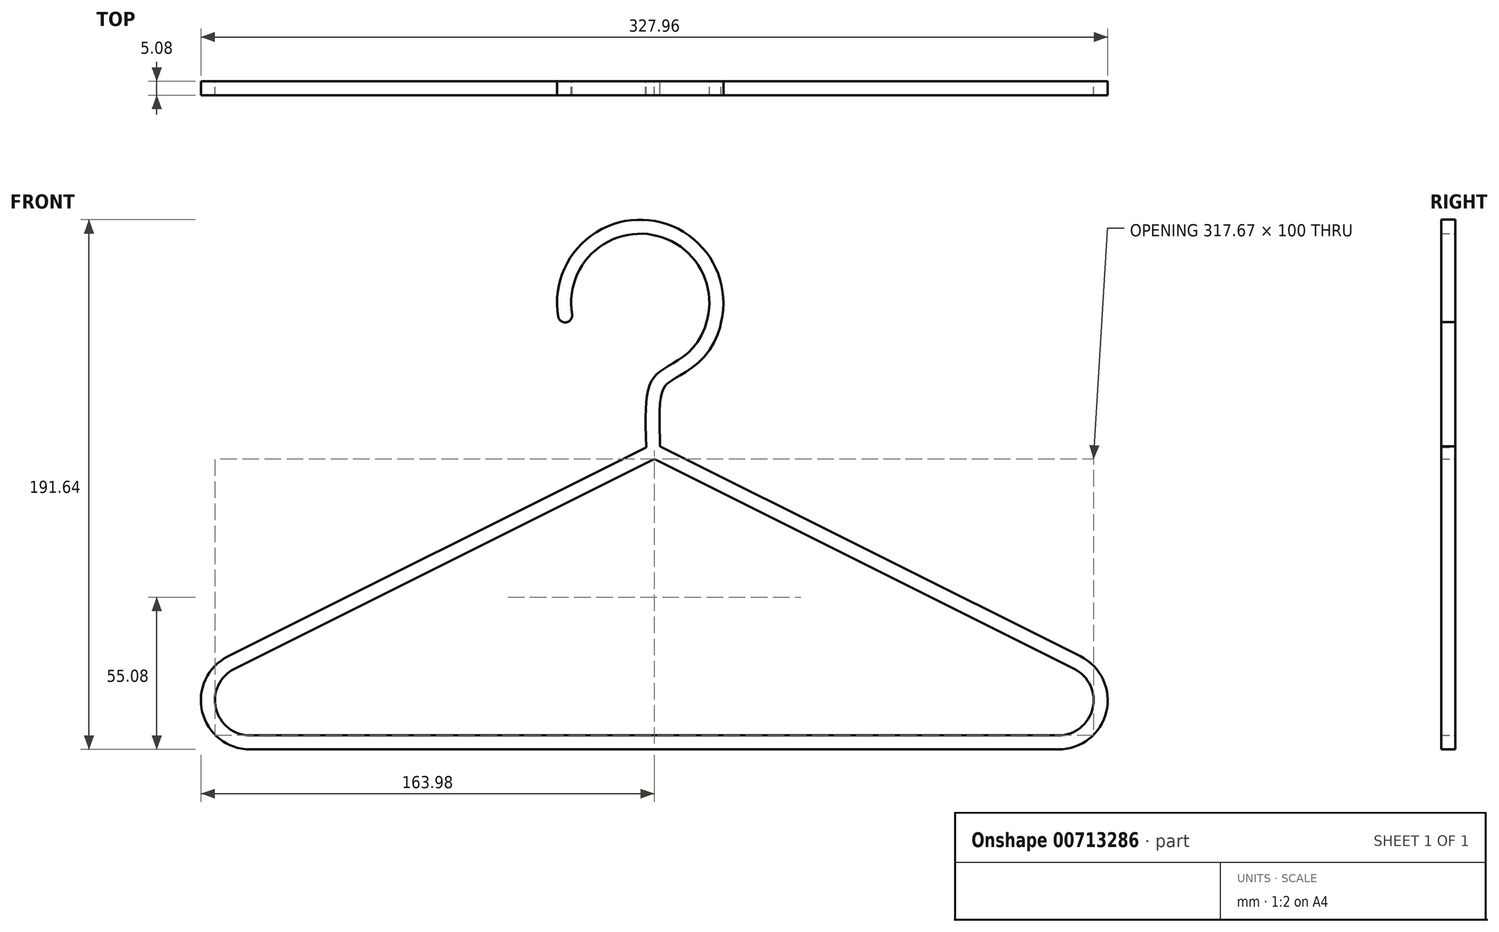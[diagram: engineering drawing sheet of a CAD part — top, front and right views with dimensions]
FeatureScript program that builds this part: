
annotation { "Feature Type Name" : "Feature", "Feature Type Description" : "" }
export const myFeature = defineFeature(function(context is Context, id is Id, definition is map)
    precondition{}
    {
        {
            var Q0;
            Q0=qCreatedBy(makeId("Front.planeOp"),FACE);
            var sketch = newSketch(context, id + "F0", { "sketchPlane" : qUnion([Q0])});
            skLineSegment(sketch, "E0", {"start": v(-146.2, 5.08) * mm, "end": v(146.2, 5.08) * mm});
            skLineSegment(sketch, "E1", {"start": v(151.88, 29.14) * mm, "end": v(0, 105.08) * mm});
            skLineSegment(sketch, "E2", {"start": v(0, 105.08) * mm, "end": v(-151.88, 29.14) * mm});
            skPoint(sketch, "E3.visualSharp", {"position": v(-200, 5.08) * mm});
            skArc(sketch, "E3.filletArc", {"start": v(-151.88, 29.14) * mm, "mid": v(-158.56, 14.86) * mm, "end": v(-146.2, 5.08) * mm});
            skPoint(sketch, "E4.visualSharp", {"position": v(200, 5.08) * mm});
            skArc(sketch, "E4.filletArc", {"start": v(146.2, 5.08) * mm, "mid": v(158.56, 14.86) * mm, "end": v(151.88, 29.14) * mm});
            skLineSegment(sketch, "E5.0", {"start": v(154.15, 33.68) * mm, "end": v(0, 110.76) * mm, "construction": true});
            skArc(sketch, "E6.0", {"start": v(146.2, 0) * mm, "mid": v(163.5, 13.7) * mm, "end": v(154.15, 33.68) * mm});
            skLineSegment(sketch, "E7.0", {"start": v(-146.2, 0) * mm, "end": v(146.2, 0) * mm});
            skArc(sketch, "E8.0", {"start": v(-154.15, 33.68) * mm, "mid": v(-163.5, 13.7) * mm, "end": v(-146.2, 0) * mm});
            skLineSegment(sketch, "E9.0", {"start": v(0, 110.76) * mm, "end": v(-154.15, 33.68) * mm, "construction": true});
            skCircle(sketch, "E10", {"center": v(-5.08, 161.56) * mm, "radius": 25 * mm, "construction": true});
            skArc(sketch, "E11", {"start": v(-29.74, 157.43) * mm, "mid": v(-4.24, 186.55) * mm, "end": v(19.25, 155.8) * mm});
            skFitSpline(sketch, "E12", {"points": [v(19.25, 155.8) * mm, v(1.59, 136.34) * mm, v(-2.96, 109.28) * mm], "startDerivative": vector(-19.16, -80.8) * mm, "endDerivative": vector(2.52, -99.4) * mm});
            skFitSpline(sketch, "E13.0", {"points": [v(24.19, 154.62) * mm, v(23.73, 152.67) * mm, v(22.54, 149.08) * mm, v(20.08, 144.64) * mm, v(17.16, 141.1) * mm, v(14.06, 138.39) * mm, v(11.03, 136.32) * mm, v(8.76, 134.97) * mm, v(7.2, 134.04) * mm, v(6.17, 133.41) * mm, v(5.48, 132.94) * mm, v(5.02, 132.59) * mm, v(4.73, 132.35) * mm, v(4.47, 132.12) * mm, v(4.17, 131.82) * mm, v(3.86, 131.45) * mm, v(3.53, 130.98) * mm, v(3.24, 130.44) * mm, v(2.97, 129.78) * mm, v(2.63, 128.7) * mm, v(2.28, 126.88) * mm, v(2.02, 123.87) * mm, v(1.9, 118.73) * mm, v(2, 113.54) * mm, v(2.11, 109.4) * mm]});
            skArc(sketch, "E14.0", {"start": v(-34.75, 156.59) * mm, "mid": v(-4.08, 191.62) * mm, "end": v(24.19, 154.62) * mm});
            skArc(sketch, "E15", {"start": v(-34.75, 156.59) * mm, "mid": v(-31.82, 154.5) * mm, "end": v(-29.74, 157.43) * mm});
            skLineSegment(sketch, "E16", {"start": v(-154.15, 33.68) * mm, "end": v(-2.96, 109.28) * mm});
            skLineSegment(sketch, "E17", {"start": v(2.1, 109.7) * mm, "end": v(154.15, 33.68) * mm});
            skSolve(sketch);
        }
        {
            var Q0;
            Q0=makeQuery(id+"F0.imprint","IMPRINT",FACE,{"disambiguationData":[TD([[makeQuery(id+"F0.imprint","IMPRINT",EDGE,{"derivedFrom":sQuery(id+"F0.wireOp",EDGE,"E0")}),-1.0]])]});
            extrude(context, id + "F1", {"entities" : qUnion([Q0]), "depth" : 5.08 * mm, "offsetDistance" : 25.4 * mm});
        }
    });
